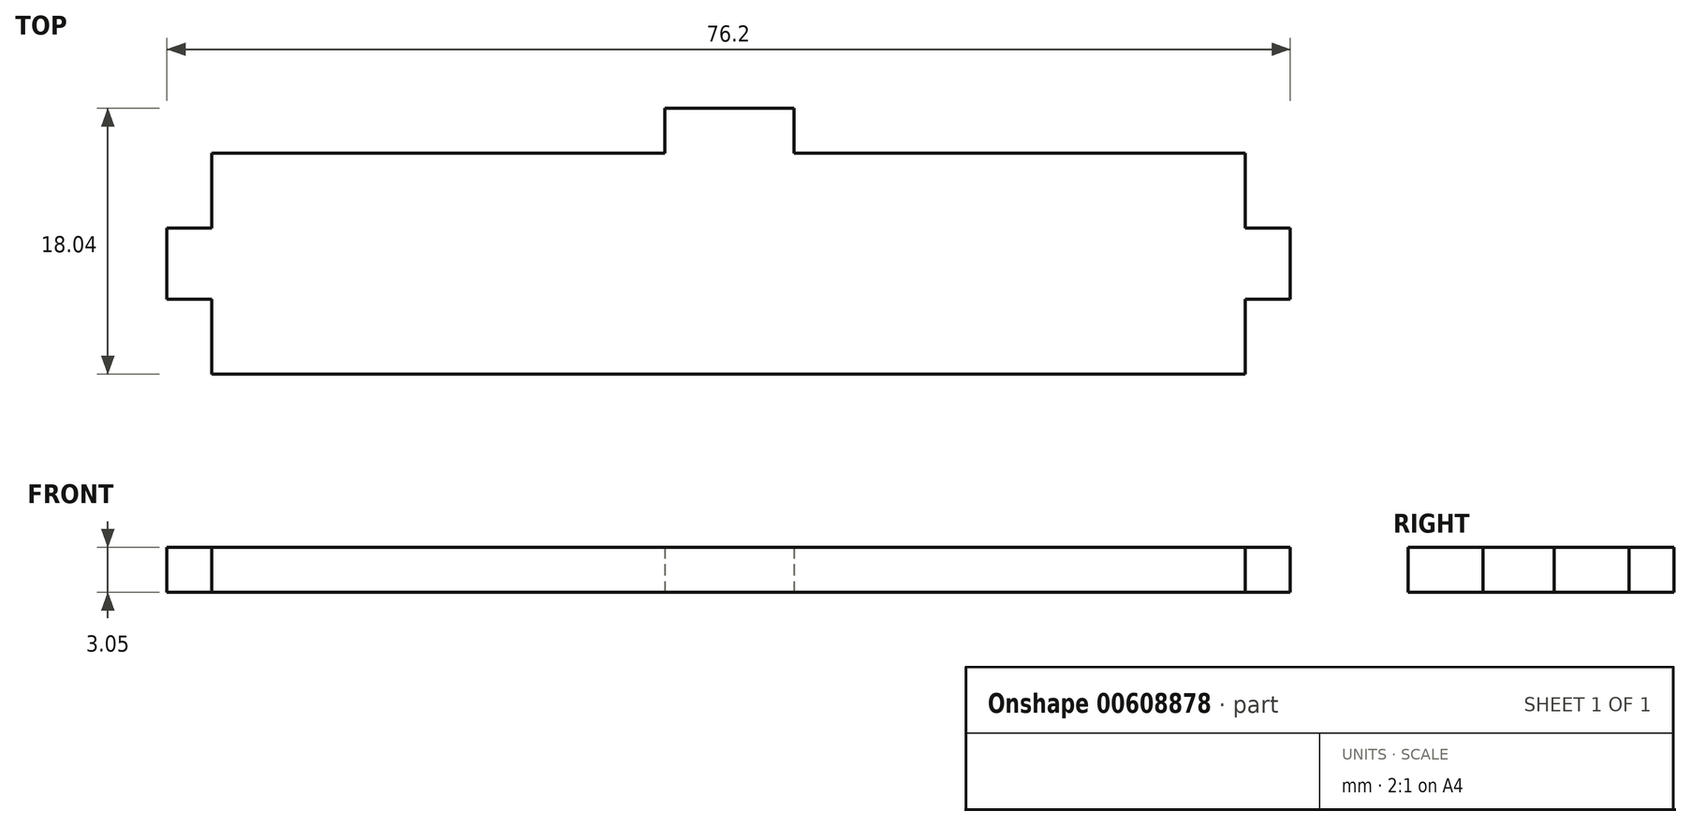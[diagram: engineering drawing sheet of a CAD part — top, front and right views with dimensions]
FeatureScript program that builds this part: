
annotation { "Feature Type Name" : "Feature", "Feature Type Description" : "" }
export const myFeature = defineFeature(function(context is Context, id is Id, definition is map)
    precondition{}
    {
        {
            var Q0;
            Q0=qCreatedBy(makeId("Top.planeOp"),FACE);
            var sketch = newSketch(context, id + "F0", { "sketchPlane" : qUnion([Q0])});
            skLineSegment(sketch, "E0.bottom", {"start": v(-4.32, 9.02) * mm, "end": v(4.44, 9.02) * mm});
            skLineSegment(sketch, "E0.top", {"start": v(-35.05, -9.02) * mm, "end": v(35.05, -9.02) * mm});
            skPoint(sketch, "E0.middle", {"position": v(0, 0) * mm});
            skLineSegment(sketch, "E1.0", {"start": v(-35.05, 5.97) * mm, "end": v(-4.32, 5.97) * mm});
            skLineSegment(sketch, "E2.0", {"start": v(35.05, 5.97) * mm, "end": v(35.05, 0.89) * mm});
            skLineSegment(sketch, "E3.0", {"start": v(-35.05, 5.97) * mm, "end": v(-35.05, 0.89) * mm});
            skLineSegment(sketch, "E4.0", {"start": v(-38.1, -3.94) * mm, "end": v(-35.05, -3.94) * mm});
            skLineSegment(sketch, "E5.0", {"start": v(-38.1, 0.89) * mm, "end": v(-35.05, 0.89) * mm});
            skLineSegment(sketch, "E6.trimOffspring", {"start": v(-38.1, 0.89) * mm, "end": v(-38.1, -3.94) * mm});
            skLineSegment(sketch, "E7.trimOffspring", {"start": v(-35.05, -3.94) * mm, "end": v(-35.05, -9.02) * mm});
            skLineSegment(sketch, "E8.trimOffspring", {"start": v(35.05, -3.94) * mm, "end": v(35.05, -9.02) * mm});
            skLineSegment(sketch, "E9.trimOffspring", {"start": v(38.1, 0.89) * mm, "end": v(38.1, -3.94) * mm});
            skLineSegment(sketch, "E10.trimOffspring", {"start": v(35.05, 0.89) * mm, "end": v(38.1, 0.89) * mm});
            skLineSegment(sketch, "E11.trimOffspring", {"start": v(35.05, -3.94) * mm, "end": v(38.1, -3.94) * mm});
            skLineSegment(sketch, "E12.0", {"start": v(4.44, 9.02) * mm, "end": v(4.44, 5.97) * mm});
            skLineSegment(sketch, "E13.0", {"start": v(-4.32, 9.02) * mm, "end": v(-4.32, 5.97) * mm});
            skLineSegment(sketch, "E14.trimOffspring", {"start": v(4.44, 5.97) * mm, "end": v(35.05, 5.97) * mm});
            skSolve(sketch);
        }
        {
            var Q0;
            Q0=makeQuery(id+"F0.imprint","IMPRINT",FACE,{"disambiguationData":[TD([[makeQuery(id+"F0.imprint","IMPRINT",EDGE,{"derivedFrom":sQuery(id+"F0.wireOp",EDGE,"E0.bottom")}),-1.0]])]});
            extrude(context, id + "F1", {"entities" : qUnion([Q0]), "depth" : 3.05 * mm, "offsetDistance" : 25.4 * mm});
        }
    });
